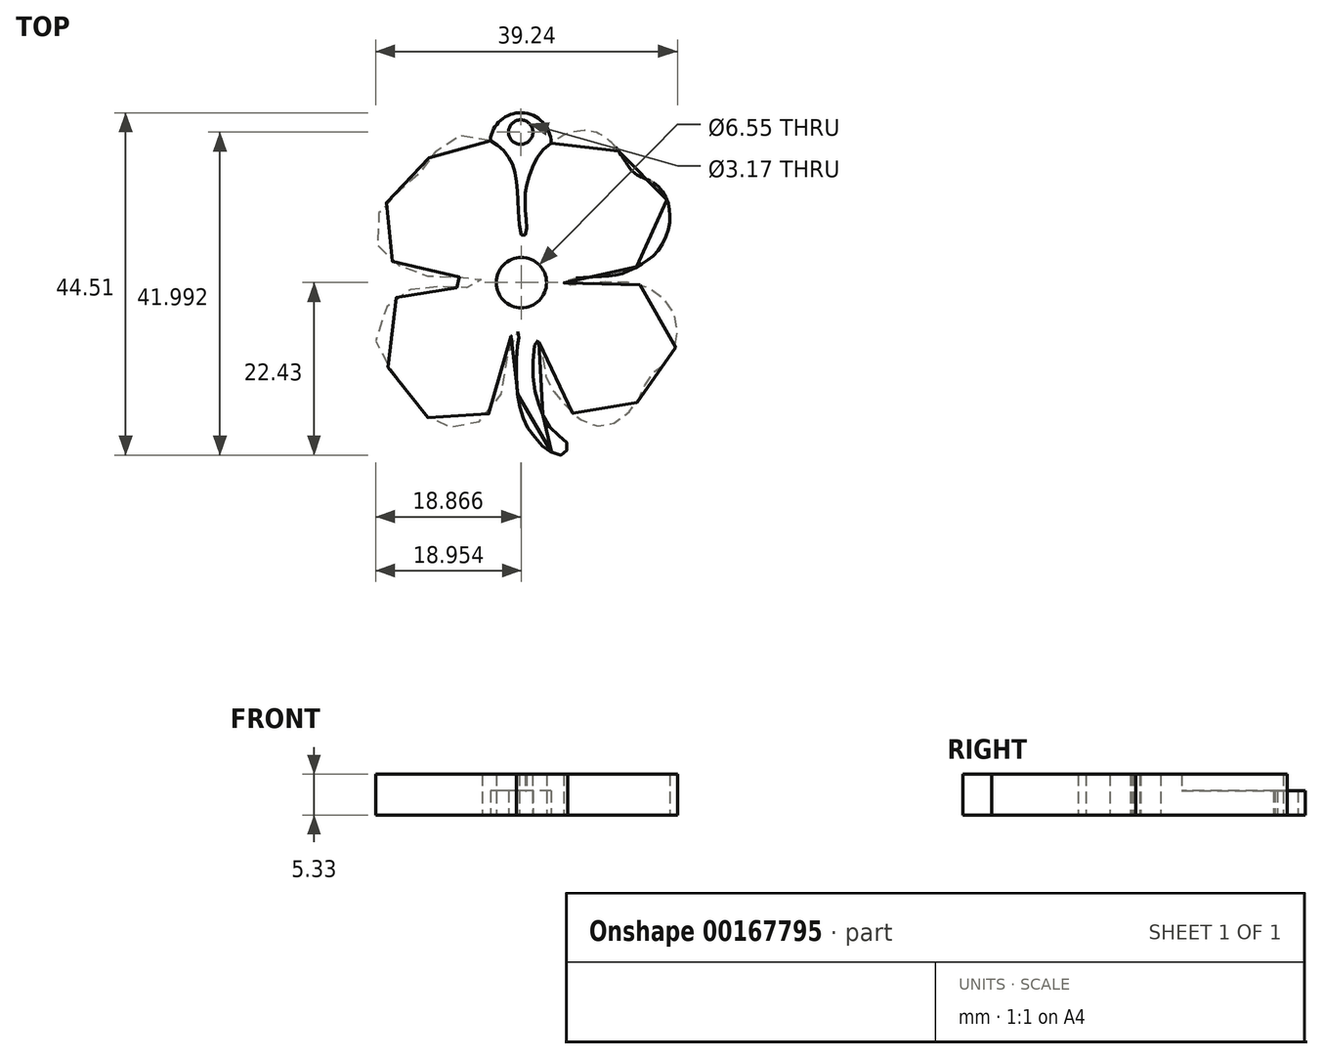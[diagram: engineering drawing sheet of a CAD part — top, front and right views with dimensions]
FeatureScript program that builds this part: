
annotation { "Feature Type Name" : "Feature", "Feature Type Description" : "" }
export const myFeature = defineFeature(function(context is Context, id is Id, definition is map)
    precondition{}
    {
        {
            var Q0;
            Q0=qCreatedBy(makeId("Top.planeOp"),FACE);
            var sketch = newSketch(context, id + "F0", { "sketchPlane" : qUnion([Q0])});
            skFitSpline(sketch, "E0", {"points": [v(0.5, 0.76) * mm, v(-0.02, 4) * mm, v(-0.14, 6.6) * mm, v(-0.42, 8.97) * mm, v(-1.05, 10.66) * mm, v(-2.11, 12.05) * mm, v(-3.65, 13.15) * mm, v(-5.31, 13.78) * mm, v(-7.32, 13.82) * mm, v(-9.06, 13.07) * mm, v(-10.44, 11.97) * mm, v(-11.82, 10.62) * mm, v(-12.42, 9.4) * mm, v(-13.28, 8.45) * mm, v(-14.03, 7.66) * mm, v(-15.18, 6.87) * mm, v(-16.92, 5.3) * mm, v(-17.98, 4.07) * mm, v(-18.38, 2.41) * mm, v(-18.47, 0.1) * mm, v(-17.84, -1.3) * mm, v(-16.57, -2.46) * mm, v(-14.5, -3.58) * mm, v(-12.84, -4.17) * mm, v(-11.21, -4.57) * mm, v(-9.83, -4.65) * mm, v(-7.4, -4.63) * mm, v(-5.88, -4.73) * mm, v(-5.02, -4.73) * mm, v(-4.73, -5.05) * mm, v(-4.75, -5.42) * mm, v(-5.32, -5.74) * mm, v(-6.55, -5.97) * mm, v(-8.54, -5.95) * mm, v(-9.92, -5.93) * mm, v(-11.28, -5.78) * mm, v(-13.16, -5.93) * mm, v(-14.45, -6.4) * mm, v(-15.85, -7.24) * mm, v(-17.26, -8.67) * mm, v(-18.36, -11.1) * mm, v(-18.47, -13.79) * mm, v(-17.44, -15.82) * mm, v(-15.48, -17.76) * mm, v(-14.87, -18.37) * mm, v(-14.3, -19.68) * mm, v(-13.64, -20.88) * mm, v(-12.38, -22.38) * mm, v(-10.98, -23.37) * mm, v(-9.44, -24.06) * mm, v(-8.22, -24.1) * mm, v(-6.49, -24.03) * mm, v(-4.58, -23) * mm, v(-3.06, -21.44) * mm, v(-1.76, -18.37) * mm, v(-1.38, -15.19) * mm, v(-1.11, -12.83) * mm, v(-0.76, -12.03) * mm, v(0.02, -11.76) * mm, v(0.08, -12.28) * mm, v(-0.09, -13.18) * mm, v(-0.26, -15.67) * mm, v(-0.09, -19.87) * mm, v(0.37, -22.22) * mm, v(1, -23.85) * mm, v(2.09, -25.4) * mm, v(3.32, -26.73) * mm, v(4.66, -27.55) * mm, v(6, -27.65) * mm, v(6.35, -26.8) * mm, v(6.25, -26.04) * mm, v(4.74, -24.83) * mm, v(3.4, -23.03) * mm, v(2.55, -20.88) * mm, v(1.92, -18.01) * mm, v(1.96, -14.65) * mm, v(2.38, -12.72) * mm, v(3.05, -14.35) * mm, v(3.45, -17.03) * mm, v(4.24, -19.02) * mm, v(5.91, -21.07) * mm, v(7.9, -23.03) * mm, v(10.2, -23.97) * mm, v(12.12, -23.74) * mm, v(14.23, -22.28) * mm, v(15.43, -20.9) * mm, v(16.18, -19.25) * mm, v(16.95, -17.78) * mm, v(18.27, -16.28) * mm, v(19.13, -15.82) * mm, v(20.49, -13.56) * mm, v(20.61, -11.13) * mm, v(20.11, -8.98) * mm, v(18.33, -6.95) * mm, v(16.05, -5.68) * mm, v(12.52, -5.24) * mm, v(9.24, -5.4) * mm, v(7.33, -5.61) * mm, v(6.29, -5.61) * mm, v(5.9, -5.32) * mm, v(6.18, -5.05) * mm, v(7.36, -4.73) * mm, v(11, -4.53) * mm, v(13.46, -4.13) * mm, v(15.95, -2.96) * mm, v(17.96, -1.4) * mm, v(19.4, 1.3) * mm, v(19.7, 3.73) * mm, v(19.21, 5.64) * mm, v(17.9, 7.46) * mm, v(16.24, 8.3) * mm, v(14.9, 9.07) * mm, v(13.8, 10.57) * mm, v(12.5, 12.45) * mm, v(11.29, 13.54) * mm, v(9.66, 14.31) * mm, v(6.98, 14.2) * mm, v(4.26, 12.83) * mm, v(2.38, 10.84) * mm, v(1.31, 8.31) * mm, v(0.92, 6.45) * mm, v(0.87, 4.61) * mm, v(1.02, 2.46) * mm, v(0.9, 0.93) * mm, v(0.5, 0.76) * mm]});
            skCircle(sketch, "E1", {"center": v(0.38, -5.32) * mm, "radius": 3.28 * mm});
            skArc(sketch, "E2", {"start": v(4.26, 12.83) * mm, "mid": v(0.46, 16.76) * mm, "end": v(-3.65, 13.15) * mm});
            skCircle(sketch, "E3", {"center": v(0.3, 14.24) * mm, "radius": 1.59 * mm});
            skSolve(sketch);
        }
        {
            var Q0;
            Q0=makeQuery(id+"F0.imprint","IMPRINT",FACE,{"disambiguationData":[TD([[makeQuery(id+"F0.imprint","IMPRINT",EDGE,{"derivedFrom":sQuery(id+"F0.wireOp",EDGE,"E0")}),1.0]])]});
            extrude(context, id + "F1", {"entities" : qUnion([Q0]), "depth" : 5.33 * mm});
        }
        {
            var Q0;
            {var subQ0=sQuery(id+"F0.wireOp",EDGE,"E2");Q0=makeQuery(id+"F0.imprint","IMPRINT",FACE,{"disambiguationData":[TD([[makeQuery(id+"F0.imprint","IMPRINT",EDGE,{"derivedFrom":subQ0}),1.0]])]});}
            extrude(context, id + "F2", {"entities" : qUnion([Q0]), "operationType" : NewBodyOperationType.ADD, "depth" : 3.17 * mm});
        }
    });
